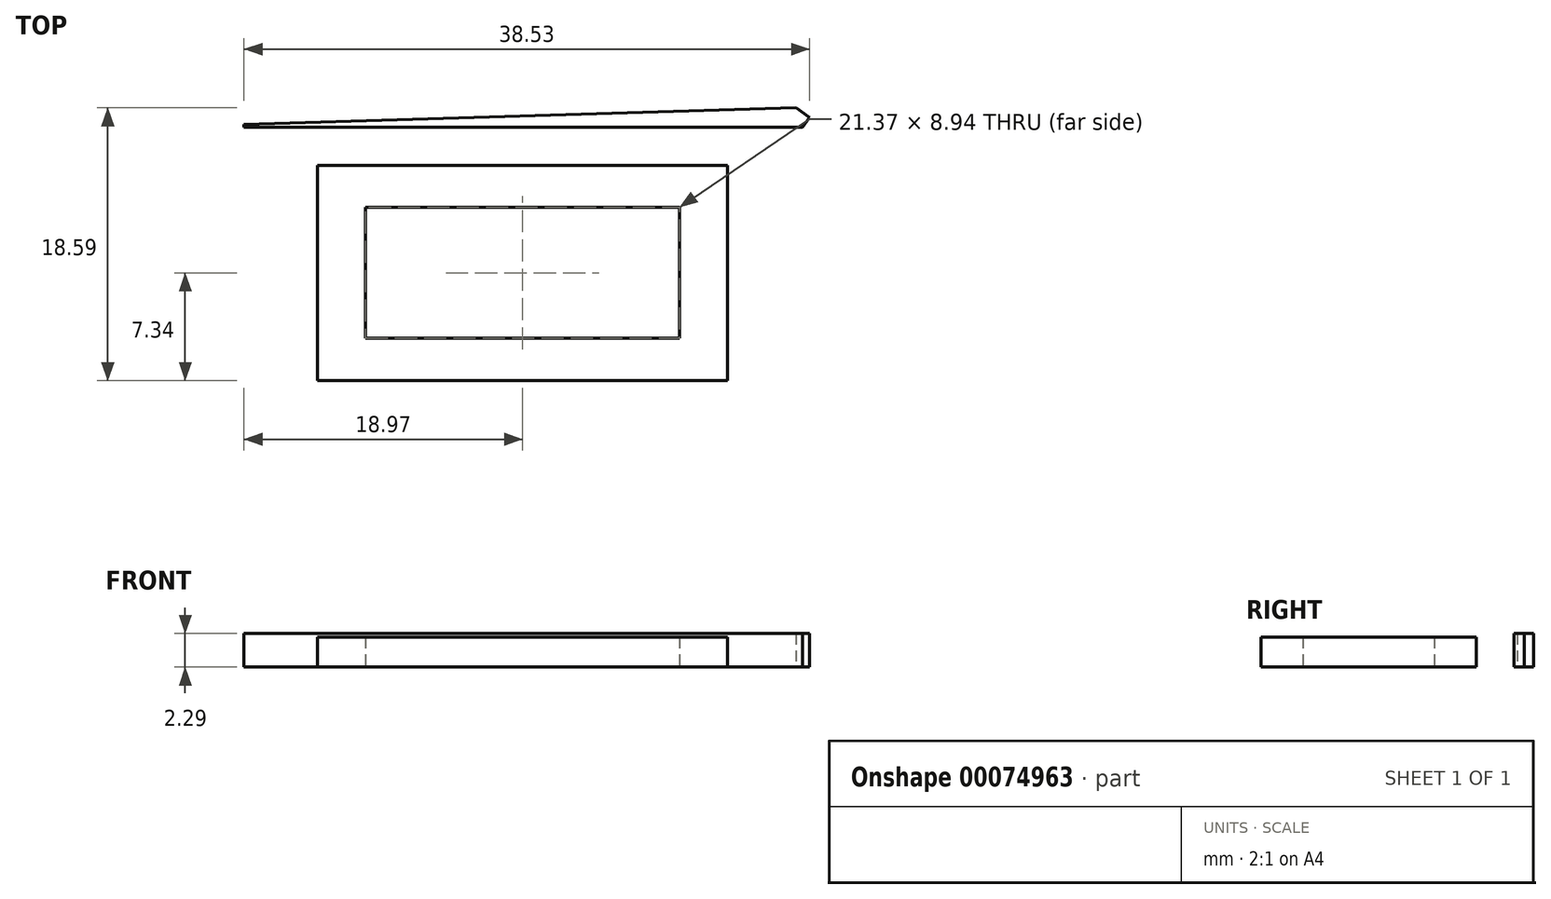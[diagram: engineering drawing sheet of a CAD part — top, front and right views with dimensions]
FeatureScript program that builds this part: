
annotation { "Feature Type Name" : "Feature", "Feature Type Description" : "" }
export const myFeature = defineFeature(function(context is Context, id is Id, definition is map)
    precondition{}
    {
        {
            var Q0;
            Q0=qCreatedBy(makeId("Top.planeOp"),FACE);
            var sketch = newSketch(context, id + "F0", { "sketchPlane" : qUnion([Q0])});
            skLineSegment(sketch, "E0.rect.bottom", {"start": v(-13.97, 7.34) * mm, "end": v(13.97, 7.34) * mm});
            skLineSegment(sketch, "E0.rect.top", {"start": v(-13.97, -7.34) * mm, "end": v(13.97, -7.34) * mm});
            skLineSegment(sketch, "E0.rect.left", {"start": v(-13.97, 7.34) * mm, "end": v(-13.97, -7.34) * mm});
            skLineSegment(sketch, "E0.rect.right", {"start": v(13.97, 7.34) * mm, "end": v(13.97, -7.34) * mm});
            skPoint(sketch, "E0.rect.middle", {"position": v(0, 0) * mm});
            skLineSegment(sketch, "E1.rect.bottom", {"start": v(-10.69, 4.47) * mm, "end": v(10.69, 4.47) * mm});
            skLineSegment(sketch, "E1.rect.top", {"start": v(-10.69, -4.47) * mm, "end": v(10.69, -4.47) * mm});
            skLineSegment(sketch, "E1.rect.left", {"start": v(-10.69, 4.47) * mm, "end": v(-10.69, -4.47) * mm});
            skLineSegment(sketch, "E1.rect.right", {"start": v(10.69, 4.47) * mm, "end": v(10.69, -4.47) * mm});
            skLineSegment(sketch, "E2.bottom", {"start": v(-18.95, 12.73) * mm, "end": v(17.8, 12.73) * mm});
            skLineSegment(sketch, "E2.top", {"start": v(-18.95, 11.3) * mm, "end": v(17.8, 11.3) * mm});
            skLineSegment(sketch, "E2.left", {"start": v(-18.95, 12.73) * mm, "end": v(-18.95, 11.3) * mm});
            skLineSegment(sketch, "E2.right", {"start": v(17.8, 12.73) * mm, "end": v(17.8, 11.3) * mm});
            skSolve(sketch);
        }
        {
            var Q0;
            Q0=makeQuery(id+"F0.imprint","IMPRINT",FACE,{"disambiguationData":[TD([[makeQuery(id+"F0.imprint","IMPRINT",EDGE,{"derivedFrom":sQuery(id+"F0.wireOp",EDGE,"E0.rect.bottom")}),-1.0]])]});
            extrude(context, id + "F1", {"entities" : qUnion([Q0]), "depth" : 2.03 * mm});
        }
        {
            var Q0;
            Q0=qCreatedBy(makeId("Top.planeOp"),FACE);
            var sketch = newSketch(context, id + "F2", { "sketchPlane" : qUnion([Q0])});
            skLineSegment(sketch, "E3", {"start": v(-18.97, 10.11) * mm, "end": v(18.64, 11.25) * mm});
            skLineSegment(sketch, "E4", {"start": v(18.64, 11.25) * mm, "end": v(19.56, 10.61) * mm});
            skLineSegment(sketch, "E5", {"start": v(19.56, 10.61) * mm, "end": v(19.09, 9.92) * mm});
            skLineSegment(sketch, "E6", {"start": v(19.09, 9.92) * mm, "end": v(-18.97, 9.92) * mm});
            skLineSegment(sketch, "E7", {"start": v(-18.97, 9.92) * mm, "end": v(-18.97, 10.11) * mm});
            skSolve(sketch);
        }
        {
            var Q0;
            Q0=makeQuery(id+"F2.imprint","IMPRINT",FACE,{"disambiguationData":[TD([[makeQuery(id+"F2.imprint","IMPRINT",EDGE,{"derivedFrom":sQuery(id+"F2.wireOp",EDGE,"E3")}),-1.0]])]});
            extrude(context, id + "F3", {"entities" : qUnion([Q0]), "depth" : 2.3 * mm});
        }
    });
